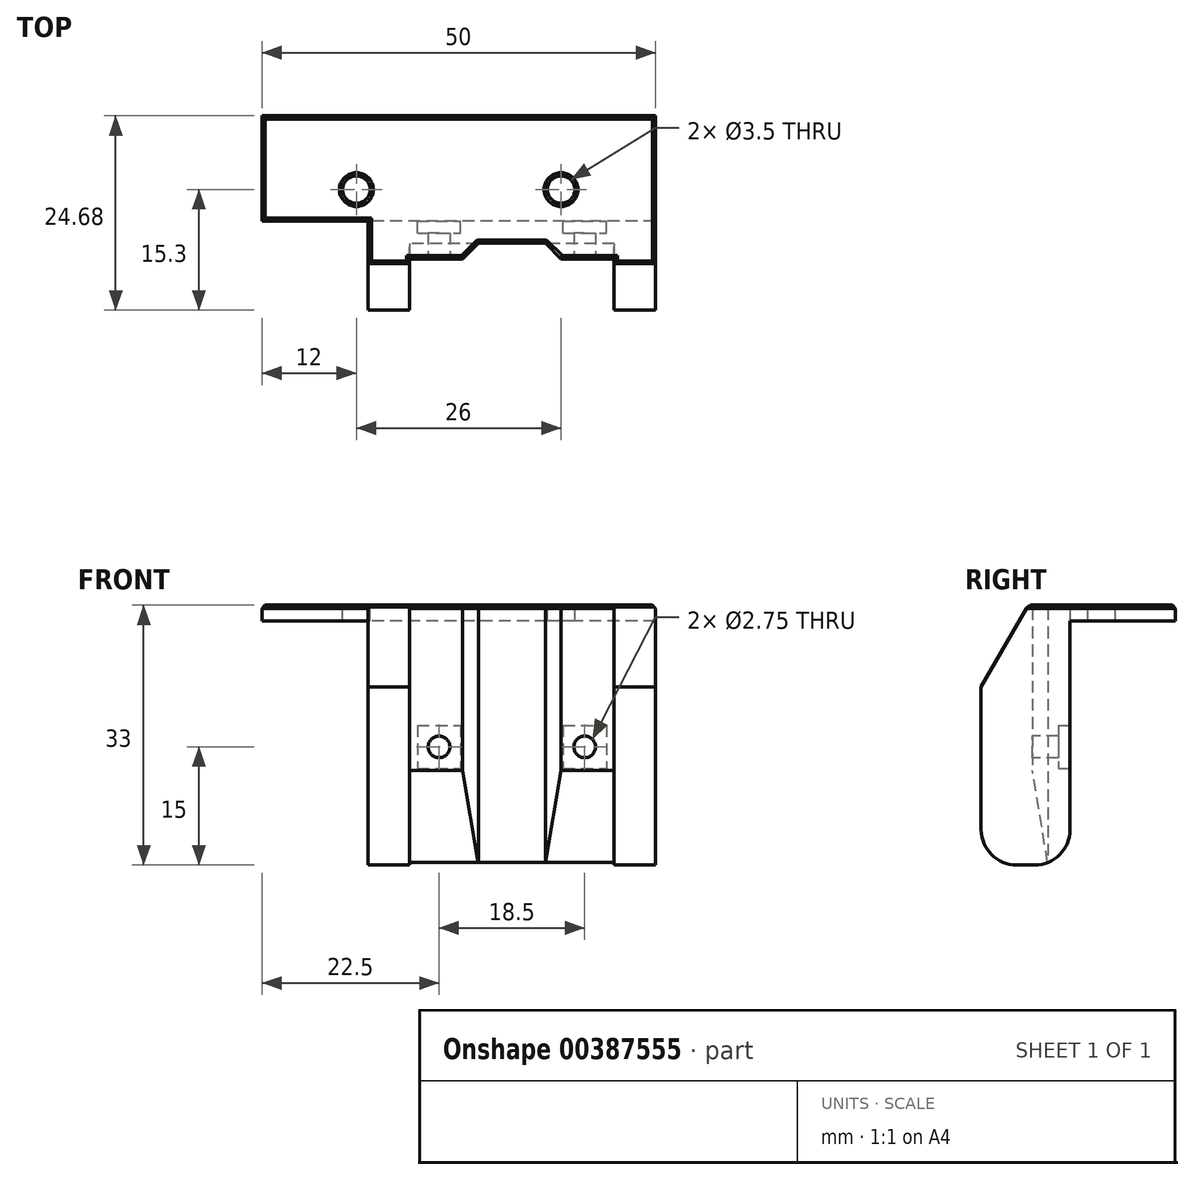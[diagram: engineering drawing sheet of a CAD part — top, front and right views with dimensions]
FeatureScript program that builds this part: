
annotation { "Feature Type Name" : "Feature", "Feature Type Description" : "" }
export const myFeature = defineFeature(function(context is Context, id is Id, definition is map)
    precondition{}
    {
        {
            var Q0;
            Q0=qCreatedBy(makeId("Right.planeOp"),FACE);
            var sketch = newSketch(context, id + "F0", { "sketchPlane" : qUnion([Q0])});
            skLineSegment(sketch, "E0", {"start": v(0, 0) * mm, "end": v(13.38, 0) * mm});
            skLineSegment(sketch, "E1", {"start": v(13.38, 0) * mm, "end": v(13.38, 2) * mm});
            skLineSegment(sketch, "E2", {"start": v(13.38, 2) * mm, "end": v(0, 2) * mm});
            skLineSegment(sketch, "E3", {"start": v(0, 2) * mm, "end": v(0, 0) * mm});
            skSolve(sketch);
        }
        {
            var Q0;
            Q0=makeQuery(id+"F0.imprint","IMPRINT",FACE,{"disambiguationData":[TD([[makeQuery(id+"F0.imprint","IMPRINT",EDGE,{"derivedFrom":sQuery(id+"F0.wireOp",EDGE,"E0")}),1.0]])]});
            extrude(context, id + "F1", {"entities" : qUnion([Q0]), "endBound" : BoundingType.SYMMETRIC, "depth" : 50 * mm});
        }
        {
            var Q0;
            Q0=makeQuery(id+"F1.opExtrude","SWEPT_FACE",FACE,{"disambiguationData":[OSD([sQuery(id+"F0.wireOp",EDGE,"E2")])]});
            var sketch = newSketch(context, id + "F2", { "sketchPlane" : qUnion([Q0])});
            skLineSegment(sketch, "E4", {"start": v(-25, 4) * mm, "end": v(25, 4) * mm, "construction": true});
            skLineSegment(sketch, "E5", {"start": v(0, 13.38) * mm, "end": v(0, 0) * mm, "construction": true});
            skCircle(sketch, "E6", {"center": v(-13, 4) * mm, "radius": 1.75 * mm});
            skCircle(sketch, "E7", {"center": v(13, 4) * mm, "radius": 1.75 * mm});
            skSolve(sketch);
        }
        {
            var Q0;
            Q0=qSketchRegion(id+"F2",true);
            extrude(context, id + "F3", {"entities" : qUnion([Q0]), "operationType" : NewBodyOperationType.REMOVE, "endBound" : BoundingType.UP_TO_NEXT, "oppositeDirection" : true, "depth" : 25 * mm});
        }
        {
            var Q0;
            Q0=qCreatedBy(makeId("Right.planeOp"),FACE);
            var sketch = newSketch(context, id + "F4", { "sketchPlane" : qUnion([Q0])});
            skLineSegment(sketch, "E8.bottom", {"start": v(0, 2) * mm, "end": v(-11.3, 2) * mm});
            skLineSegment(sketch, "E8.top", {"start": v(0, -31) * mm, "end": v(-11.3, -31) * mm});
            skLineSegment(sketch, "E8.left", {"start": v(0, 2) * mm, "end": v(0, -31) * mm});
            skLineSegment(sketch, "E8.right", {"start": v(-11.3, 2) * mm, "end": v(-11.3, -31) * mm});
            skSolve(sketch);
        }
        {
            var Q0;
            Q0=qSketchRegion(id+"F4",true);
            var Q1;
            Q1=makeQuery(id+"F1.opExtrude","CAP_FACE",FACE,{"disambiguationData":[OSD([sQuery(id+"F0.wireOp",EDGE,"E0"),sQuery(id+"F0.wireOp",EDGE,"E1"),sQuery(id+"F0.wireOp",EDGE,"E2"),sQuery(id+"F0.wireOp",EDGE,"E3")])],"isStart":false});
            extrude(context, id + "F5", {"entities" : qUnion([Q0]), "operationType" : NewBodyOperationType.ADD, "endBound" : BoundingType.UP_TO_SURFACE, "endBoundEntityFace" : qUnion([Q1]), "depth" : 36.5 * mm, "hasSecondDirection" : true, "secondDirectionOppositeDirection" : true, "secondDirectionDepth" : 11.5 * mm});
        }
        {
            var Q0;
            Q0=makeQuery(id+"F5.opExtrude","SWEPT_FACE",FACE,{"disambiguationData":[OSD([sQuery(id+"F4.wireOp",EDGE,"E8.top")])]});
            var sketch = newSketch(context, id + "F6", { "sketchPlane" : qUnion([Q0])});
            skLineSegment(sketch, "E9.bottom", {"start": v(-6.25, 11.3) * mm, "end": v(19.75, 11.3) * mm});
            skLineSegment(sketch, "E9.top", {"start": v(-6.25, 4.8) * mm, "end": v(19.75, 4.8) * mm});
            skLineSegment(sketch, "E9.left", {"start": v(-6.25, 11.3) * mm, "end": v(-6.25, 4.8) * mm});
            skLineSegment(sketch, "E9.right", {"start": v(19.75, 11.3) * mm, "end": v(19.75, 4.8) * mm});
            skLineSegment(sketch, "E10", {"start": v(6.75, 11.3) * mm, "end": v(6.75, 0) * mm, "construction": true});
            skSolve(sketch);
        }
        {
            var Q0;
            Q0=qSketchRegion(id+"F6",true);
            extrude(context, id + "F7", {"entities" : qUnion([Q0]), "operationType" : NewBodyOperationType.REMOVE, "endBound" : BoundingType.UP_TO_NEXT, "oppositeDirection" : true, "depth" : 25 * mm});
        }
        {
            var Q0;
            Q0=makeQuery(id+"F5.opExtrude","SWEPT_FACE",FACE,{"disambiguationData":[OSD([sQuery(id+"F4.wireOp",EDGE,"E8.top")])]});
            var sketch = newSketch(context, id + "F8", { "sketchPlane" : qUnion([Q0])});
            skLineSegment(sketch, "E11", {"start": v(6.75, 4.8) * mm, "end": v(6.75, 0) * mm, "construction": true});
            skLineSegment(sketch, "E12", {"start": v(0.5, 4.8) * mm, "end": v(2.5, 2.8) * mm});
            skLineSegment(sketch, "E13", {"start": v(2.5, 2.8) * mm, "end": v(11, 2.8) * mm});
            skLineSegment(sketch, "E14", {"start": v(11, 2.8) * mm, "end": v(13, 4.8) * mm});
            skLineSegment(sketch, "E15", {"start": v(13, 4.8) * mm, "end": v(0.5, 4.8) * mm});
            skSolve(sketch);
        }
        {
            var Q0;
            Q0=qSketchRegion(id+"F8",true);
            extrude(context, id + "F9", {"entities" : qUnion([Q0]), "operationType" : NewBodyOperationType.REMOVE, "endBound" : BoundingType.UP_TO_NEXT, "oppositeDirection" : true, "depth" : 25 * mm});
        }
        {
            var Q0;
            Q0=qCreatedBy(makeId("Right.planeOp"),FACE);
            var sketch = newSketch(context, id + "F10", { "sketchPlane" : qUnion([Q0])});
            skLineSegment(sketch, "E16", {"start": v(-2.8, -31) * mm, "end": v(-4.8, -19) * mm});
            skLineSegment(sketch, "E17", {"start": v(-4.8, -19) * mm, "end": v(-4.8, -31) * mm});
            skLineSegment(sketch, "E18", {"start": v(-4.8, -31) * mm, "end": v(-2.8, -31) * mm});
            skSolve(sketch);
        }
        {
            var Q0;
            Q0=qSketchRegion(id+"F10",true);
            var Q1;
            Q1=makeQuery(id+"F7.boolean.opBoolean","COPY",FACE,{"derivedFrom":makeQuery(id+"F7.opExtrude","SWEPT_FACE",FACE,{"disambiguationData":[OSD([sQuery(id+"F6.wireOp",EDGE,"E9.right")])]})});
            var Q2;
            Q2=makeQuery(id+"F7.boolean.opBoolean","COPY",FACE,{"derivedFrom":makeQuery(id+"F7.opExtrude","SWEPT_FACE",FACE,{"disambiguationData":[OSD([sQuery(id+"F6.wireOp",EDGE,"E9.left")])]})});
            extrude(context, id + "F11", {"entities" : qUnion([Q0]), "operationType" : NewBodyOperationType.REMOVE, "endBound" : BoundingType.UP_TO_SURFACE, "endBoundEntityFace" : qUnion([Q1]), "depth" : 25 * mm, "hasSecondDirection" : true, "secondDirectionBound" : SecondDirectionBoundingType.UP_TO_SURFACE, "secondDirectionOppositeDirection" : true, "secondDirectionBoundEntityFace" : qUnion([Q2]), "secondDirectionDepth" : 25 * mm});
        }
        {
            var Q0;
            Q0=makeQuery(id+"F9.boolean.opBoolean","SPLIT",FACE,{"disambiguationData":[TD([makeQuery(id+"F7.boolean.opBoolean","COPY",FACE,{"derivedFrom":makeQuery(id+"F7.opExtrude","SWEPT_FACE",FACE,{"disambiguationData":[OSD([sQuery(id+"F6.wireOp",EDGE,"E9.left")])]})})])],"derivedFrom":makeQuery(id+"F7.boolean.opBoolean","COPY",FACE,{"derivedFrom":makeQuery(id+"F7.opExtrude","SWEPT_FACE",FACE,{"disambiguationData":[OSD([sQuery(id+"F6.wireOp",EDGE,"E9.top")])]})})});
            var sketch = newSketch(context, id + "F12", { "sketchPlane" : qUnion([Q0])});
            skCircle(sketch, "E19", {"center": v(-2.5, -16) * mm, "radius": 1.38 * mm});
            skLineSegment(sketch, "E20", {"start": v(6.75, 2) * mm, "end": v(6.75, -31) * mm, "construction": true});
            skCircle(sketch, "E21.MirrorC", {"center": v(16, -16) * mm, "radius": 1.38 * mm});
            skSolve(sketch);
        }
        {
            var Q0;
            Q0=qSketchRegion(id+"F12",true);
            extrude(context, id + "F13", {"entities" : qUnion([Q0]), "operationType" : NewBodyOperationType.REMOVE, "endBound" : BoundingType.UP_TO_NEXT, "oppositeDirection" : true, "depth" : 25 * mm});
        }
        {
            var Q0;
            Q0=makeQuery(id+"F5.opExtrude","SWEPT_FACE",FACE,{"disambiguationData":[OSD([sQuery(id+"F4.wireOp",EDGE,"E8.left")])]});
            var sketch = newSketch(context, id + "F14", { "sketchPlane" : qUnion([Q0])});
            skLineSegment(sketch, "E22.bottom", {"start": v(-13.25, -13.25) * mm, "end": v(-18.75, -13.25) * mm});
            skLineSegment(sketch, "E22.top", {"start": v(-13.25, -18.75) * mm, "end": v(-18.75, -18.75) * mm});
            skLineSegment(sketch, "E22.left", {"start": v(-13.25, -13.25) * mm, "end": v(-13.25, -18.75) * mm});
            skLineSegment(sketch, "E22.right", {"start": v(-18.75, -13.25) * mm, "end": v(-18.75, -18.75) * mm});
            skPoint(sketch, "E22.middle", {"position": v(-16, -16) * mm});
            skLineSegment(sketch, "E23.bottom", {"start": v(5.25, -13.25) * mm, "end": v(-0.25, -13.25) * mm});
            skLineSegment(sketch, "E23.top", {"start": v(5.25, -18.75) * mm, "end": v(-0.25, -18.75) * mm});
            skLineSegment(sketch, "E23.left", {"start": v(5.25, -13.25) * mm, "end": v(5.25, -18.75) * mm});
            skLineSegment(sketch, "E23.right", {"start": v(-0.25, -13.25) * mm, "end": v(-0.25, -18.75) * mm});
            skPoint(sketch, "E23.middle", {"position": v(2.5, -16) * mm});
            skSolve(sketch);
        }
        {
            var Q0;
            Q0=qSketchRegion(id+"F14",true);
            extrude(context, id + "F15", {"entities" : qUnion([Q0]), "operationType" : NewBodyOperationType.REMOVE, "oppositeDirection" : true, "depth" : 1.5 * mm});
        }
        {
            var Q0;
            {var subQ0=sQuery(id+"F4.wireOp",EDGE,"E8.right");var subQ1=sQuery(id+"F4.wireOp",EDGE,"E8.top");Q0=makeQuery(id+"F7.boolean.opBoolean","SPLIT",EDGE,{"disambiguationData":[TD([makeQuery(id+"F7.opExtrude","SWEPT_FACE",FACE,{"disambiguationData":[OSD([sQuery(id+"F6.wireOp",EDGE,"E9.left")])]})])],"derivedFrom":makeQuery(id+"F5.opExtrude","SWEPT_EDGE",EDGE,{"disambiguationData":[OSD([subQ1,subQ0])]})});}
            var Q1;
            {var subQ0=sQuery(id+"F4.wireOp",EDGE,"E8.right");var subQ1=sQuery(id+"F4.wireOp",EDGE,"E8.top");Q1=makeQuery(id+"F7.boolean.opBoolean","SPLIT",EDGE,{"disambiguationData":[TD([makeQuery(id+"F7.opExtrude","SWEPT_FACE",FACE,{"disambiguationData":[OSD([sQuery(id+"F6.wireOp",EDGE,"E9.right")])]})])],"derivedFrom":makeQuery(id+"F5.opExtrude","SWEPT_EDGE",EDGE,{"disambiguationData":[OSD([subQ1,subQ0])]})});}
            var Q2;
            Q2=makeQuery(id+"F5.opExtrude","SWEPT_EDGE",EDGE,{"disambiguationData":[OSD([sQuery(id+"F4.wireOp",EDGE,"E8.top"),sQuery(id+"F4.wireOp",EDGE,"E8.left")])]});
            fillet(context, id + "F16", {"entities" : qUnion([Q0, Q1, Q2]), "radius" : 4.5 * mm, "tangentPropagation" : true, "allowEdgeOverflow" : false});
        }
        {
            var Q0;
            {var subQ0=sQuery(id+"F4.wireOp",EDGE,"E8.right");var subQ1=sQuery(id+"F4.wireOp",EDGE,"E8.bottom");Q0=makeQuery(id+"F7.boolean.opBoolean","SPLIT",EDGE,{"disambiguationData":[TD([makeQuery(id+"F7.opExtrude","SWEPT_FACE",FACE,{"disambiguationData":[OSD([sQuery(id+"F6.wireOp",EDGE,"E9.left")])]})])],"derivedFrom":makeQuery(id+"F5.opExtrude","SWEPT_EDGE",EDGE,{"disambiguationData":[OSD([subQ1,subQ0])]})});}
            var Q1;
            {var subQ0=sQuery(id+"F4.wireOp",EDGE,"E8.right");var subQ1=sQuery(id+"F4.wireOp",EDGE,"E8.bottom");Q1=makeQuery(id+"F7.boolean.opBoolean","SPLIT",EDGE,{"disambiguationData":[TD([makeQuery(id+"F7.opExtrude","SWEPT_FACE",FACE,{"disambiguationData":[OSD([sQuery(id+"F6.wireOp",EDGE,"E9.right")])]})])],"derivedFrom":makeQuery(id+"F5.opExtrude","SWEPT_EDGE",EDGE,{"disambiguationData":[OSD([subQ1,subQ0])]})});}
            chamfer(context, id + "F17", {"entities" : qUnion([Q0, Q1]), "chamferType" : ChamferType.OFFSET_ANGLE, "width" : 6 * mm, "oppositeDirection" : true, "angle" : 60 * degree, "tangentPropagation" : true});
        }
        {
            var Q0;
            Q0=makeQuery(id+"F5.boolean.opBoolean","MERGE",FACE,{"derivedFrom":[makeQuery(id+"F1.opExtrude","SWEPT_FACE",FACE,{"disambiguationData":[OSD([sQuery(id+"F0.wireOp",EDGE,"E2")])]}),makeQuery(id+"F5.opExtrude","SWEPT_FACE",FACE,{"disambiguationData":[OSD([sQuery(id+"F4.wireOp",EDGE,"E8.bottom")])]})]});
            chamfer(context, id + "F18", {"entities" : qUnion([Q0]), "width" : 0.4 * mm, "tangentPropagation" : true});
        }
    });
